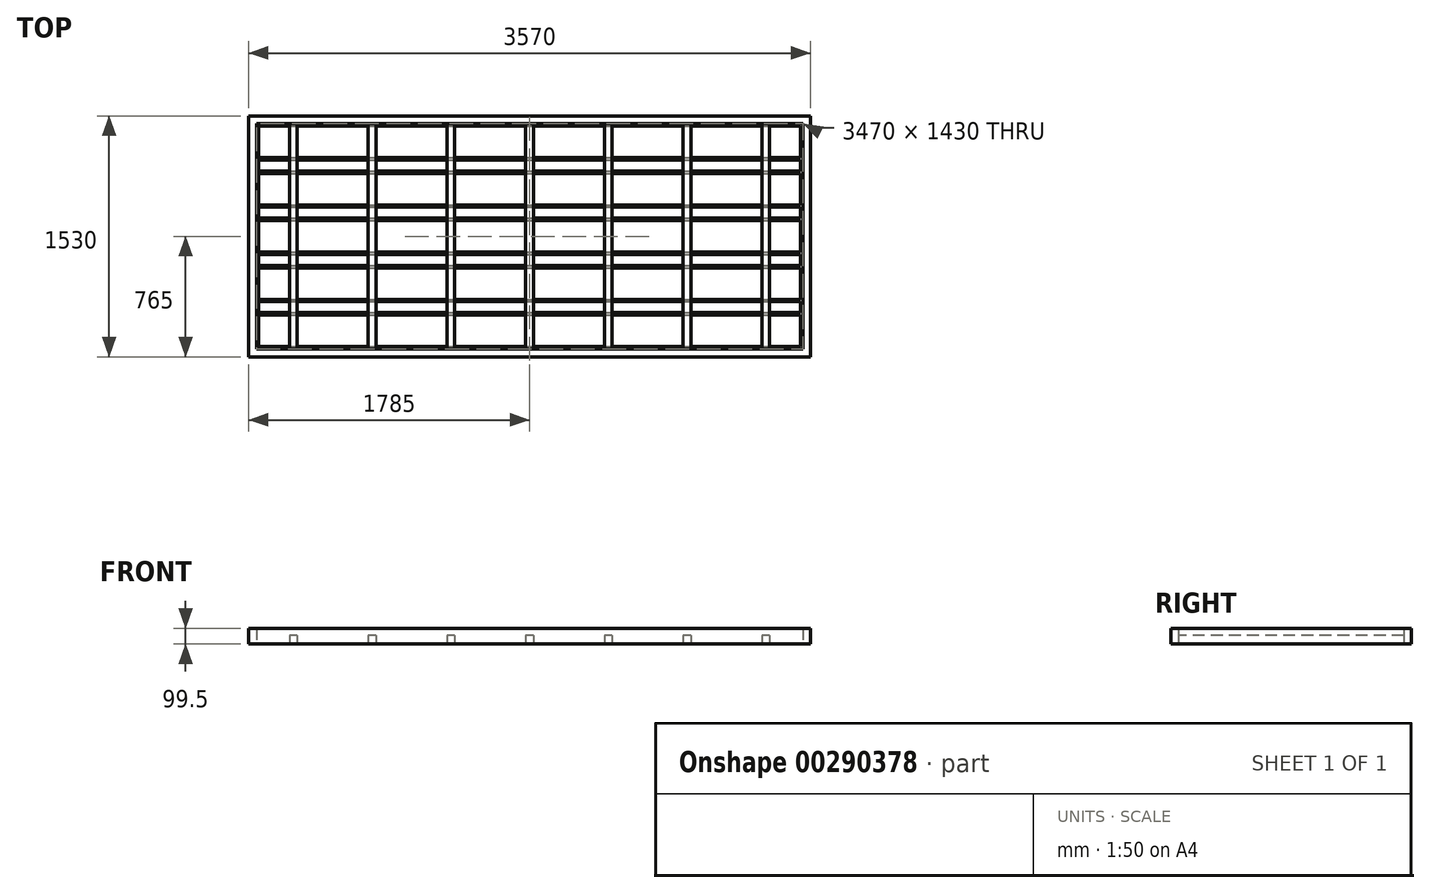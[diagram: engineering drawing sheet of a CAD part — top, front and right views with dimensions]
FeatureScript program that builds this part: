
annotation { "Feature Type Name" : "Feature", "Feature Type Description" : "" }
export const myFeature = defineFeature(function(context is Context, id is Id, definition is map)
    precondition{}
    {
        {
            var Q0;
            Q0=qCreatedBy(makeId("Top.planeOp"),FACE);
            var sketch = newSketch(context, id + "F0", { "sketchPlane" : qUnion([Q0])});
            skLineSegment(sketch, "E0.bottom", {"start": v(0, 0) * mm, "end": v(3570, 0) * mm});
            skLineSegment(sketch, "E0.top", {"start": v(0, 1530) * mm, "end": v(3570, 1530) * mm});
            skLineSegment(sketch, "E0.left", {"start": v(0, 0) * mm, "end": v(0, 1530) * mm});
            skLineSegment(sketch, "E0.right", {"start": v(3570, 0) * mm, "end": v(3570, 1530) * mm});
            skLineSegment(sketch, "E1.0", {"start": v(50, 1480) * mm, "end": v(3520, 1480) * mm});
            skLineSegment(sketch, "E1.1", {"start": v(50, 50) * mm, "end": v(50, 1480) * mm});
            skLineSegment(sketch, "E1.2", {"start": v(50, 50) * mm, "end": v(3520, 50) * mm});
            skLineSegment(sketch, "E1.3", {"start": v(3520, 50) * mm, "end": v(3520, 1480) * mm});
            skLineSegment(sketch, "E2.bottom", {"start": v(65, 350) * mm, "end": v(3505, 350) * mm});
            skLineSegment(sketch, "E2.top", {"start": v(65, 280) * mm, "end": v(3505, 280) * mm});
            skLineSegment(sketch, "E2.left", {"start": v(65, 350) * mm, "end": v(65, 280) * mm});
            skLineSegment(sketch, "E2.right", {"start": v(3505, 350) * mm, "end": v(3505, 280) * mm});
            skLineSegment(sketch, "E3.bottom", {"start": v(65, 65) * mm, "end": v(3505, 65) * mm});
            skLineSegment(sketch, "E3.top", {"start": v(65, 265) * mm, "end": v(3505, 265) * mm});
            skLineSegment(sketch, "E3.left", {"start": v(65, 65) * mm, "end": v(65, 265) * mm});
            skLineSegment(sketch, "E3.right", {"start": v(3505, 65) * mm, "end": v(3505, 265) * mm});
            skLineSegment(sketch, "E4.0.1.0", {"start": v(65, 580) * mm, "end": v(3505, 580) * mm});
            skLineSegment(sketch, "E4.0.1.1", {"start": v(65, 650) * mm, "end": v(3505, 650) * mm});
            skLineSegment(sketch, "E4.0.1.2", {"start": v(65, 650) * mm, "end": v(65, 580) * mm});
            skLineSegment(sketch, "E4.0.1.3", {"start": v(3505, 650) * mm, "end": v(3505, 580) * mm});
            skLineSegment(sketch, "E4.0.2.0", {"start": v(65, 880) * mm, "end": v(3505, 880) * mm});
            skLineSegment(sketch, "E4.0.2.1", {"start": v(65, 950) * mm, "end": v(3505, 950) * mm});
            skLineSegment(sketch, "E4.0.2.2", {"start": v(65, 950) * mm, "end": v(65, 880) * mm});
            skLineSegment(sketch, "E4.0.2.3", {"start": v(3505, 950) * mm, "end": v(3505, 880) * mm});
            skLineSegment(sketch, "E4.0.3.0", {"start": v(65, 1180) * mm, "end": v(3505, 1180) * mm});
            skLineSegment(sketch, "E4.0.3.1", {"start": v(65, 1250) * mm, "end": v(3505, 1250) * mm});
            skLineSegment(sketch, "E4.0.3.2", {"start": v(65, 1250) * mm, "end": v(65, 1180) * mm});
            skLineSegment(sketch, "E4.0.3.3", {"start": v(3505, 1250) * mm, "end": v(3505, 1180) * mm});
            skLineSegment(sketch, "E4.direction1", {"start": v(65, 280) * mm, "end": v(90, 280) * mm, "construction": true});
            skLineSegment(sketch, "E4.direction2", {"start": v(65, 280) * mm, "end": v(65, 580) * mm, "construction": true});
            skLineSegment(sketch, "E5.0.1.0", {"start": v(65, 565) * mm, "end": v(3505, 565) * mm});
            skLineSegment(sketch, "E5.0.1.1", {"start": v(3505, 365) * mm, "end": v(3505, 565) * mm});
            skLineSegment(sketch, "E5.0.1.2", {"start": v(65, 365) * mm, "end": v(3505, 365) * mm});
            skLineSegment(sketch, "E5.0.1.3", {"start": v(65, 365) * mm, "end": v(65, 565) * mm});
            skLineSegment(sketch, "E5.0.2.0", {"start": v(65, 865) * mm, "end": v(3505, 865) * mm});
            skLineSegment(sketch, "E5.0.2.1", {"start": v(3505, 665) * mm, "end": v(3505, 865) * mm});
            skLineSegment(sketch, "E5.0.2.2", {"start": v(65, 665) * mm, "end": v(3505, 665) * mm});
            skLineSegment(sketch, "E5.0.2.3", {"start": v(65, 665) * mm, "end": v(65, 865) * mm});
            skLineSegment(sketch, "E5.0.3.0", {"start": v(65, 1165) * mm, "end": v(3505, 1165) * mm});
            skLineSegment(sketch, "E5.0.3.1", {"start": v(3505, 965) * mm, "end": v(3505, 1165) * mm});
            skLineSegment(sketch, "E5.0.3.2", {"start": v(65, 965) * mm, "end": v(3505, 965) * mm});
            skLineSegment(sketch, "E5.0.3.3", {"start": v(65, 965) * mm, "end": v(65, 1165) * mm});
            skLineSegment(sketch, "E5.0.4.0", {"start": v(65, 1465) * mm, "end": v(3505, 1465) * mm});
            skLineSegment(sketch, "E5.0.4.1", {"start": v(3505, 1265) * mm, "end": v(3505, 1465) * mm});
            skLineSegment(sketch, "E5.0.4.2", {"start": v(65, 1265) * mm, "end": v(3505, 1265) * mm});
            skLineSegment(sketch, "E5.0.4.3", {"start": v(65, 1265) * mm, "end": v(65, 1465) * mm});
            skLineSegment(sketch, "E5.direction1", {"start": v(65, 65) * mm, "end": v(90, 65) * mm, "construction": true});
            skLineSegment(sketch, "E5.direction2", {"start": v(65, 65) * mm, "end": v(65, 365) * mm, "construction": true});
            skSolve(sketch);
        }
        {
            var Q0;
            Q0=makeQuery(id+"F0.imprint","IMPRINT",FACE,{"disambiguationData":[TD([[makeQuery(id+"F0.imprint","IMPRINT",EDGE,{"derivedFrom":sQuery(id+"F0.wireOp",EDGE,"E4.0.2.0")}),1.0]])]});
            var Q1;
            Q1=makeQuery(id+"F0.imprint","IMPRINT",FACE,{"disambiguationData":[TD([[makeQuery(id+"F0.imprint","IMPRINT",EDGE,{"derivedFrom":sQuery(id+"F0.wireOp",EDGE,"E4.0.3.0")}),1.0]])]});
            var Q2;
            Q2=makeQuery(id+"F0.imprint","IMPRINT",FACE,{"disambiguationData":[TD([[makeQuery(id+"F0.imprint","IMPRINT",EDGE,{"derivedFrom":sQuery(id+"F0.wireOp",EDGE,"E4.0.1.0")}),1.0]])]});
            var Q3;
            Q3=makeQuery(id+"F0.imprint","IMPRINT",FACE,{"disambiguationData":[TD([[makeQuery(id+"F0.imprint","IMPRINT",EDGE,{"derivedFrom":sQuery(id+"F0.wireOp",EDGE,"E2.bottom")}),-1.0]])]});
            var Q4;
            Q4=makeQuery(id+"F0.imprint","IMPRINT",FACE,{"disambiguationData":[TD([[makeQuery(id+"F0.imprint","IMPRINT",EDGE,{"derivedFrom":sQuery(id+"F0.wireOp",EDGE,"E5.0.4.0")}),-1.0]])]});
            var Q5;
            Q5=makeQuery(id+"F0.imprint","IMPRINT",FACE,{"disambiguationData":[TD([[makeQuery(id+"F0.imprint","IMPRINT",EDGE,{"derivedFrom":sQuery(id+"F0.wireOp",EDGE,"E5.0.3.0")}),-1.0]])]});
            var Q6;
            Q6=makeQuery(id+"F0.imprint","IMPRINT",FACE,{"disambiguationData":[TD([[makeQuery(id+"F0.imprint","IMPRINT",EDGE,{"derivedFrom":sQuery(id+"F0.wireOp",EDGE,"E5.0.2.0")}),-1.0]])]});
            var Q7;
            Q7=makeQuery(id+"F0.imprint","IMPRINT",FACE,{"disambiguationData":[TD([[makeQuery(id+"F0.imprint","IMPRINT",EDGE,{"derivedFrom":sQuery(id+"F0.wireOp",EDGE,"E5.0.1.0")}),-1.0]])]});
            var Q8;
            Q8=makeQuery(id+"F0.imprint","IMPRINT",FACE,{"disambiguationData":[TD([[makeQuery(id+"F0.imprint","IMPRINT",EDGE,{"derivedFrom":sQuery(id+"F0.wireOp",EDGE,"E3.bottom")}),1.0]])]});
            extrude(context, id + "F1", {"entities" : qUnion([Q0, Q1, Q2, Q3, Q4, Q5, Q6, Q7, Q8]), "depth" : 5 * mm});
        }
        {
            var Q0;
            Q0=qSketchRegion(id+"F0",true);
            var Q1;
            Q1=makeQuery(id+"F1.opExtrude","CAP_FACE",FACE,{"disambiguationData":[OSD([sQuery(id+"F0.wireOp",EDGE,"E0.bottom"),sQuery(id+"F0.wireOp",EDGE,"E0.top"),sQuery(id+"F0.wireOp",EDGE,"E0.left"),sQuery(id+"F0.wireOp",EDGE,"E0.right"),sQuery(id+"F0.wireOp",EDGE,"E1.0"),sQuery(id+"F0.wireOp",EDGE,"E1.1"),sQuery(id+"F0.wireOp",EDGE,"E1.2"),sQuery(id+"F0.wireOp",EDGE,"E1.3")])],"isStart":false});
            extrude(context, id + "F2", {"entities" : qUnion([Q0, Q1]), "depth" : 99.5 * mm});
        }
        {
            var Q0;
            Q0=makeQuery(id+"F1.opExtrude","CAP_FACE",FACE,{"disambiguationData":[OSD([sQuery(id+"F0.wireOp",EDGE,"E5.0.4.0"),sQuery(id+"F0.wireOp",EDGE,"E5.0.4.1"),sQuery(id+"F0.wireOp",EDGE,"E5.0.4.2"),sQuery(id+"F0.wireOp",EDGE,"E5.0.4.3")])],"isStart":false});
            var sketch = newSketch(context, id + "F3", { "sketchPlane" : qUnion([Q0])});
            skLineSegment(sketch, "E6.bottom", {"start": v(310, 50) * mm, "end": v(260, 50) * mm});
            skLineSegment(sketch, "E6.top", {"start": v(310, 1480) * mm, "end": v(260, 1480) * mm});
            skLineSegment(sketch, "E6.left", {"start": v(310, 1480) * mm, "end": v(310, 50) * mm});
            skLineSegment(sketch, "E6.right", {"start": v(260, 1480) * mm, "end": v(260, 50) * mm});
            skLineSegment(sketch, "E7.1.0.0", {"start": v(810, 1480) * mm, "end": v(760, 1480) * mm});
            skLineSegment(sketch, "E7.1.0.1", {"start": v(760, 1480) * mm, "end": v(760, 50) * mm});
            skLineSegment(sketch, "E7.1.0.2", {"start": v(810, 50) * mm, "end": v(760, 50) * mm});
            skLineSegment(sketch, "E7.1.0.3", {"start": v(810, 1480) * mm, "end": v(810, 50) * mm});
            skLineSegment(sketch, "E7.2.0.0", {"start": v(1310, 1480) * mm, "end": v(1260, 1480) * mm});
            skLineSegment(sketch, "E7.2.0.1", {"start": v(1260, 1480) * mm, "end": v(1260, 50) * mm});
            skLineSegment(sketch, "E7.2.0.2", {"start": v(1310, 50) * mm, "end": v(1260, 50) * mm});
            skLineSegment(sketch, "E7.2.0.3", {"start": v(1310, 1480) * mm, "end": v(1310, 50) * mm});
            skLineSegment(sketch, "E7.3.0.0", {"start": v(1810, 1480) * mm, "end": v(1760, 1480) * mm});
            skLineSegment(sketch, "E7.3.0.1", {"start": v(1760, 1480) * mm, "end": v(1760, 50) * mm});
            skLineSegment(sketch, "E7.3.0.2", {"start": v(1810, 50) * mm, "end": v(1760, 50) * mm});
            skLineSegment(sketch, "E7.3.0.3", {"start": v(1810, 1480) * mm, "end": v(1810, 50) * mm});
            skLineSegment(sketch, "E7.direction1", {"start": v(310, 50) * mm, "end": v(810, 50) * mm, "construction": true});
            skLineSegment(sketch, "E8.0.4.0", {"start": v(2310, 1480) * mm, "end": v(2260, 1480) * mm});
            skLineSegment(sketch, "E8.3.4.0", {"start": v(2260, 1480) * mm, "end": v(2260, 50) * mm});
            skLineSegment(sketch, "E8.6.4.0", {"start": v(2310, 50) * mm, "end": v(2260, 50) * mm});
            skLineSegment(sketch, "E8.9.4.0", {"start": v(2310, 1480) * mm, "end": v(2310, 50) * mm});
            skLineSegment(sketch, "E8.0.5.0", {"start": v(2810, 1480) * mm, "end": v(2760, 1480) * mm});
            skLineSegment(sketch, "E8.3.5.0", {"start": v(2760, 1480) * mm, "end": v(2760, 50) * mm});
            skLineSegment(sketch, "E8.6.5.0", {"start": v(2810, 50) * mm, "end": v(2760, 50) * mm});
            skLineSegment(sketch, "E8.9.5.0", {"start": v(2810, 1480) * mm, "end": v(2810, 50) * mm});
            skLineSegment(sketch, "E9.0.6.0", {"start": v(3310, 1480) * mm, "end": v(3260, 1480) * mm});
            skLineSegment(sketch, "E9.3.6.0", {"start": v(3260, 1480) * mm, "end": v(3260, 50) * mm});
            skLineSegment(sketch, "E9.6.6.0", {"start": v(3310, 50) * mm, "end": v(3260, 50) * mm});
            skLineSegment(sketch, "E9.9.6.0", {"start": v(3310, 1480) * mm, "end": v(3310, 50) * mm});
            skSolve(sketch);
        }
        {
            var Q0;
            {var subQ0=sQuery(id+"F3.wireOp",EDGE,"E6.bottom");Q0=makeQuery(id+"F3.imprint","IMPRINT",FACE,{"disambiguationData":[TD([[makeQuery(id+"F3.imprint","IMPRINT",EDGE,{"derivedFrom":subQ0}),1.0]])]});}
            var Q1;
            {var subQ0=sQuery(id+"F3.wireOp",EDGE,"E7.1.0.2");Q1=makeQuery(id+"F3.imprint","IMPRINT",FACE,{"disambiguationData":[TD([[makeQuery(id+"F3.imprint","IMPRINT",EDGE,{"derivedFrom":subQ0}),1.0]])]});}
            var Q2;
            {var subQ0=sQuery(id+"F3.wireOp",EDGE,"E7.2.0.2");Q2=makeQuery(id+"F3.imprint","IMPRINT",FACE,{"disambiguationData":[TD([[makeQuery(id+"F3.imprint","IMPRINT",EDGE,{"derivedFrom":subQ0}),1.0]])]});}
            var Q3;
            {var subQ0=sQuery(id+"F3.wireOp",EDGE,"E7.3.0.2");Q3=makeQuery(id+"F3.imprint","IMPRINT",FACE,{"disambiguationData":[TD([[makeQuery(id+"F3.imprint","IMPRINT",EDGE,{"derivedFrom":subQ0}),1.0]])]});}
            var Q4;
            {var subQ0=sQuery(id+"F3.wireOp",EDGE,"E7.3.0.1");var subQ1=makeQuery(id+"F1.opExtrude","CAP_EDGE",EDGE,{"disambiguationData":[OSD([sQuery(id+"F0.wireOp",EDGE,"E5.0.4.2")])],"isStart":false});var subQ2=makeQuery(id+"F3.imprint","INTERSECT",VERTEX,{"derivedFrom":[subQ1,subQ0]});Q4=makeQuery(id+"F3.imprint","IMPRINT",FACE,{"disambiguationData":[TD([[makeQuery(id+"F3.imprint","IMPRINT",EDGE,{"disambiguationData":[TD([[subQ2,-1.0]])],"derivedFrom":subQ0}),1.0]])]});}
            var Q5;
            {var subQ0=sQuery(id+"F3.wireOp",EDGE,"E7.2.0.1");var subQ1=makeQuery(id+"F1.opExtrude","CAP_EDGE",EDGE,{"disambiguationData":[OSD([sQuery(id+"F0.wireOp",EDGE,"E5.0.4.2")])],"isStart":false});var subQ2=makeQuery(id+"F3.imprint","INTERSECT",VERTEX,{"derivedFrom":[subQ1,subQ0]});Q5=makeQuery(id+"F3.imprint","IMPRINT",FACE,{"disambiguationData":[TD([[makeQuery(id+"F3.imprint","IMPRINT",EDGE,{"disambiguationData":[TD([[subQ2,-1.0]])],"derivedFrom":subQ0}),1.0]])]});}
            var Q6;
            {var subQ0=sQuery(id+"F3.wireOp",EDGE,"E7.1.0.1");var subQ1=makeQuery(id+"F1.opExtrude","CAP_EDGE",EDGE,{"disambiguationData":[OSD([sQuery(id+"F0.wireOp",EDGE,"E5.0.4.2")])],"isStart":false});var subQ2=makeQuery(id+"F3.imprint","INTERSECT",VERTEX,{"derivedFrom":[subQ1,subQ0]});Q6=makeQuery(id+"F3.imprint","IMPRINT",FACE,{"disambiguationData":[TD([[makeQuery(id+"F3.imprint","IMPRINT",EDGE,{"disambiguationData":[TD([[subQ2,-1.0]])],"derivedFrom":subQ0}),1.0]])]});}
            var Q7;
            {var subQ0=sQuery(id+"F3.wireOp",EDGE,"E6.left");var subQ1=makeQuery(id+"F1.opExtrude","CAP_EDGE",EDGE,{"disambiguationData":[OSD([sQuery(id+"F0.wireOp",EDGE,"E5.0.4.2")])],"isStart":false});var subQ2=makeQuery(id+"F3.imprint","INTERSECT",VERTEX,{"derivedFrom":[subQ1,subQ0]});Q7=makeQuery(id+"F3.imprint","IMPRINT",FACE,{"disambiguationData":[TD([[makeQuery(id+"F3.imprint","IMPRINT",EDGE,{"disambiguationData":[TD([[subQ2,-1.0]])],"derivedFrom":subQ0}),-1.0]])]});}
            var Q8;
            {var subQ0=sQuery(id+"F3.wireOp",EDGE,"E6.top");Q8=makeQuery(id+"F3.imprint","IMPRINT",FACE,{"disambiguationData":[TD([[makeQuery(id+"F3.imprint","IMPRINT",EDGE,{"derivedFrom":subQ0}),-1.0]])]});}
            var Q9;
            {var subQ0=sQuery(id+"F3.wireOp",EDGE,"E7.1.0.0");Q9=makeQuery(id+"F3.imprint","IMPRINT",FACE,{"disambiguationData":[TD([[makeQuery(id+"F3.imprint","IMPRINT",EDGE,{"derivedFrom":subQ0}),-1.0]])]});}
            var Q10;
            {var subQ0=sQuery(id+"F3.wireOp",EDGE,"E7.2.0.0");Q10=makeQuery(id+"F3.imprint","IMPRINT",FACE,{"disambiguationData":[TD([[makeQuery(id+"F3.imprint","IMPRINT",EDGE,{"derivedFrom":subQ0}),-1.0]])]});}
            var Q11;
            {var subQ0=sQuery(id+"F3.wireOp",EDGE,"E7.3.0.0");Q11=makeQuery(id+"F3.imprint","IMPRINT",FACE,{"disambiguationData":[TD([[makeQuery(id+"F3.imprint","IMPRINT",EDGE,{"derivedFrom":subQ0}),-1.0]])]});}
            var Q12;
            {var subQ0=sQuery(id+"F3.wireOp",EDGE,"E6.left");var subQ1=makeQuery(id+"F1.opExtrude","CAP_EDGE",EDGE,{"disambiguationData":[OSD([sQuery(id+"F0.wireOp",EDGE,"E5.0.4.0")])],"isStart":false});var subQ2=makeQuery(id+"F3.imprint","INTERSECT",VERTEX,{"derivedFrom":[subQ1,subQ0]});Q12=makeQuery(id+"F3.imprint","IMPRINT",FACE,{"disambiguationData":[TD([[makeQuery(id+"F3.imprint","IMPRINT",EDGE,{"disambiguationData":[TD([[subQ2,-1.0]])],"derivedFrom":subQ0}),-1.0]])]});}
            var Q13;
            {var subQ0=sQuery(id+"F3.wireOp",EDGE,"E8.6.4.0");Q13=makeQuery(id+"F3.imprint","IMPRINT",FACE,{"disambiguationData":[TD([[makeQuery(id+"F3.imprint","IMPRINT",EDGE,{"derivedFrom":subQ0}),-1.0]])]});}
            var Q14;
            {var subQ0=sQuery(id+"F3.wireOp",EDGE,"E8.3.4.0");var subQ1=makeQuery(id+"F1.opExtrude","CAP_EDGE",EDGE,{"disambiguationData":[OSD([sQuery(id+"F0.wireOp",EDGE,"E5.0.4.0")])],"isStart":false});var subQ2=makeQuery(id+"F3.imprint","INTERSECT",VERTEX,{"derivedFrom":[subQ1,subQ0]});Q14=makeQuery(id+"F3.imprint","IMPRINT",FACE,{"disambiguationData":[TD([[makeQuery(id+"F3.imprint","IMPRINT",EDGE,{"disambiguationData":[TD([[subQ2,-1.0]])],"derivedFrom":subQ0}),1.0]])]});}
            var Q15;
            {var subQ0=sQuery(id+"F3.wireOp",EDGE,"E8.3.5.0");var subQ1=makeQuery(id+"F1.opExtrude","CAP_EDGE",EDGE,{"disambiguationData":[OSD([sQuery(id+"F0.wireOp",EDGE,"E5.0.4.0")])],"isStart":false});var subQ2=makeQuery(id+"F3.imprint","INTERSECT",VERTEX,{"derivedFrom":[subQ1,subQ0]});Q15=makeQuery(id+"F3.imprint","IMPRINT",FACE,{"disambiguationData":[TD([[makeQuery(id+"F3.imprint","IMPRINT",EDGE,{"disambiguationData":[TD([[subQ2,-1.0]])],"derivedFrom":subQ0}),1.0]])]});}
            var Q16;
            {var subQ0=sQuery(id+"F3.wireOp",EDGE,"E9.3.6.0");var subQ1=makeQuery(id+"F1.opExtrude","CAP_EDGE",EDGE,{"disambiguationData":[OSD([sQuery(id+"F0.wireOp",EDGE,"E5.0.4.0")])],"isStart":false});var subQ2=makeQuery(id+"F3.imprint","INTERSECT",VERTEX,{"derivedFrom":[subQ1,subQ0]});Q16=makeQuery(id+"F3.imprint","IMPRINT",FACE,{"disambiguationData":[TD([[makeQuery(id+"F3.imprint","IMPRINT",EDGE,{"disambiguationData":[TD([[subQ2,-1.0]])],"derivedFrom":subQ0}),1.0]])]});}
            var Q17;
            {var subQ0=sQuery(id+"F3.wireOp",EDGE,"E8.6.5.0");Q17=makeQuery(id+"F3.imprint","IMPRINT",FACE,{"disambiguationData":[TD([[makeQuery(id+"F3.imprint","IMPRINT",EDGE,{"derivedFrom":subQ0}),-1.0]])]});}
            var Q18;
            {var subQ0=sQuery(id+"F3.wireOp",EDGE,"E9.6.6.0");Q18=makeQuery(id+"F3.imprint","IMPRINT",FACE,{"disambiguationData":[TD([[makeQuery(id+"F3.imprint","IMPRINT",EDGE,{"derivedFrom":subQ0}),-1.0]])]});}
            var Q19;
            {var subQ0=sQuery(id+"F3.wireOp",EDGE,"E7.3.0.1");var subQ1=makeQuery(id+"F1.opExtrude","CAP_EDGE",EDGE,{"disambiguationData":[OSD([sQuery(id+"F0.wireOp",EDGE,"E5.0.4.0")])],"isStart":false});var subQ2=makeQuery(id+"F3.imprint","INTERSECT",VERTEX,{"derivedFrom":[subQ1,subQ0]});Q19=makeQuery(id+"F3.imprint","IMPRINT",FACE,{"disambiguationData":[TD([[makeQuery(id+"F3.imprint","IMPRINT",EDGE,{"disambiguationData":[TD([[subQ2,-1.0]])],"derivedFrom":subQ0}),1.0]])]});}
            var Q20;
            {var subQ0=sQuery(id+"F3.wireOp",EDGE,"E7.2.0.1");var subQ1=makeQuery(id+"F1.opExtrude","CAP_EDGE",EDGE,{"disambiguationData":[OSD([sQuery(id+"F0.wireOp",EDGE,"E5.0.4.0")])],"isStart":false});var subQ2=makeQuery(id+"F3.imprint","INTERSECT",VERTEX,{"derivedFrom":[subQ1,subQ0]});Q20=makeQuery(id+"F3.imprint","IMPRINT",FACE,{"disambiguationData":[TD([[makeQuery(id+"F3.imprint","IMPRINT",EDGE,{"disambiguationData":[TD([[subQ2,-1.0]])],"derivedFrom":subQ0}),1.0]])]});}
            var Q21;
            {var subQ0=sQuery(id+"F3.wireOp",EDGE,"E7.1.0.1");var subQ1=makeQuery(id+"F1.opExtrude","CAP_EDGE",EDGE,{"disambiguationData":[OSD([sQuery(id+"F0.wireOp",EDGE,"E5.0.4.0")])],"isStart":false});var subQ2=makeQuery(id+"F3.imprint","INTERSECT",VERTEX,{"derivedFrom":[subQ1,subQ0]});Q21=makeQuery(id+"F3.imprint","IMPRINT",FACE,{"disambiguationData":[TD([[makeQuery(id+"F3.imprint","IMPRINT",EDGE,{"disambiguationData":[TD([[subQ2,-1.0]])],"derivedFrom":subQ0}),1.0]])]});}
            var Q22;
            {var subQ0=sQuery(id+"F3.wireOp",EDGE,"E6.top");Q22=makeQuery(id+"F3.imprint","IMPRINT",FACE,{"disambiguationData":[TD([[makeQuery(id+"F3.imprint","IMPRINT",EDGE,{"derivedFrom":subQ0}),1.0]])]});}
            var Q23;
            {var subQ0=sQuery(id+"F3.wireOp",EDGE,"E7.2.0.0");Q23=makeQuery(id+"F3.imprint","IMPRINT",FACE,{"disambiguationData":[TD([[makeQuery(id+"F3.imprint","IMPRINT",EDGE,{"derivedFrom":subQ0}),1.0]])]});}
            var Q24;
            {var subQ0=sQuery(id+"F3.wireOp",EDGE,"E7.1.0.0");Q24=makeQuery(id+"F3.imprint","IMPRINT",FACE,{"disambiguationData":[TD([[makeQuery(id+"F3.imprint","IMPRINT",EDGE,{"derivedFrom":subQ0}),1.0]])]});}
            var Q25;
            {var subQ0=sQuery(id+"F3.wireOp",EDGE,"E7.3.0.0");Q25=makeQuery(id+"F3.imprint","IMPRINT",FACE,{"disambiguationData":[TD([[makeQuery(id+"F3.imprint","IMPRINT",EDGE,{"derivedFrom":subQ0}),1.0]])]});}
            var Q26;
            {var subQ0=sQuery(id+"F3.wireOp",EDGE,"E9.0.6.0");Q26=makeQuery(id+"F3.imprint","IMPRINT",FACE,{"disambiguationData":[TD([[makeQuery(id+"F3.imprint","IMPRINT",EDGE,{"derivedFrom":subQ0}),1.0]])]});}
            var Q27;
            {var subQ0=sQuery(id+"F3.wireOp",EDGE,"E8.0.4.0");Q27=makeQuery(id+"F3.imprint","IMPRINT",FACE,{"disambiguationData":[TD([[makeQuery(id+"F3.imprint","IMPRINT",EDGE,{"derivedFrom":subQ0}),1.0]])]});}
            var Q28;
            {var subQ0=sQuery(id+"F3.wireOp",EDGE,"E8.0.5.0");Q28=makeQuery(id+"F3.imprint","IMPRINT",FACE,{"disambiguationData":[TD([[makeQuery(id+"F3.imprint","IMPRINT",EDGE,{"derivedFrom":subQ0}),1.0]])]});}
            extrude(context, id + "F4", {"entities" : qUnion([Q0, Q1, Q2, Q3, Q4, Q5, Q6, Q7, Q8, Q9, Q10, Q11, Q12, Q13, Q14, Q15, Q16, Q17, Q18, Q19, Q20, Q21, Q22, Q23, Q24, Q25, Q26, Q27, Q28]), "depth" : 50 * mm});
        }
    });
